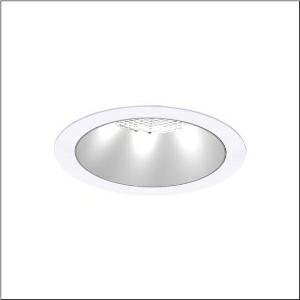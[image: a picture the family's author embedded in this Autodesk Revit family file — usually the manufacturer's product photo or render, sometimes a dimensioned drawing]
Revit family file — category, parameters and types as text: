
# Revit family: lunis_21_xl_51db19mf91c
name_source: partatom
category: Lighting Fixtures
units: mm (PartAtom-declared; Revit-internal decimal feet)

## family parameters
Cut with Voids When Loaded = No
Host = Face
Light Source = No
Part Type = Normal
Room Calculation Point = No
Round Connector Dimension = Use Diameter
Shared = No

## types (1)
- --- (1 x LED, 3560 lm, 21.7 W, 6500K)
    Apparent Load = 22 VA
    CIE Flux Codes = 91 99 100 100 100
    Color Rendering = 80
    Color Temperature = 6500K
    Default Elevation = 1800 mm
    Description = Lunis 21,  XL, downlight, light control with lens, of PMMA, anti glare with reflector, of PC, matt, light emission: direct distribution, LED rated luminous flux: 2.390lm, light colour: 830/840/865, with terminal, 3-pole, mains connection: 220..240V, AC/DC, 0/50..60Hz, housing, round, of diecast aluminium, traffic white (RAL 9016), diameter: 230mm, clamping range: 1..40mm, protection rating (complete): IP20, protection rating (on room side): IP54, insulation class (complete): insulation class II (safety insulation), certification: CE, impact resistance: IK03, packaging unit: 1 piece
    Height = 0 mm  [stored 0 ft]
    Lamp = 1 x LED
    Lamp Light Flux = 3560 lm
    Lamp Power = 21.7 W
    Lamp count = 1
    Length = 230 mm
    Luminous efficacy = 164 lm/W
    Manufacturer = Siteco
    ModVariant = No
    Model = 51DB19MF91C
    Mounting Place = Ceiling
    Mounting Type = Recessed
    Number of Poles = 1
    OnlyDefault = Yes
    Power Factor = 1
    Product Name = Lunis 21 XL
    Product group = downlight
    ProductGroupID = 400
    Protection Class = Protection class II
    Protection Degree = IP 20
    RLX_Detail_Level = 1
    RLX_Emergency_Light_Flux = 0 lm
    RLX_Emergency_Type = 0
    RLX_Emergency_Type_DB = No
    RlxData = <blob elided: 20909 chars, md5=d78c0fe3>
    Socket = socket
    Standby Power = 0 W
    System Light Flux = 3560 lm
    System Power = 22 W
    Type Comments = individual setting: colour temperature 6500K, luminous flux: 100 % | (OFF | ON | ON | ON) | 650 mA
    Type Image = l_1291163.jpg
    URL = http://relux.com
    VarID = @adj_018796
    Voltage = 0 V
    Weight = 0.00 kg
    Width = 0 mm  [stored 0 ft]

note: [stored X ft] marks values corroborated as IEEE doubles in the binary element streams (Revit-internal decimal feet)

## geometry (parser evidence)
native form markers: Blend x4, Sweep x10
no freeform markers — native parametric forms only
